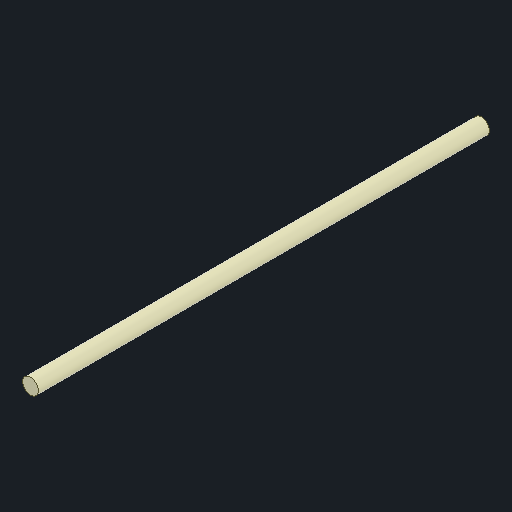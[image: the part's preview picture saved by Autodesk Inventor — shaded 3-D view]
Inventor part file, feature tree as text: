
AUTODESK INVENTOR PART (.ipt)
format: ipt  version: 2025.3 (Build 293356030, 356C)  size: 210,944 bytes
history: native  units: mm
features: other x1, extrude x1, sketch x1
ambient origin geometry x8: Origin, YZ Plane, XZ Plane, XY Plane, X Axis, Y Axis, Z Axis, Center Point
bodies: Body1 (feature_tree)
feature tree (3):
  other  "實體1"
  extrude  "擠出1"  Depth=26.5mm
  sketch  "草圖1"
